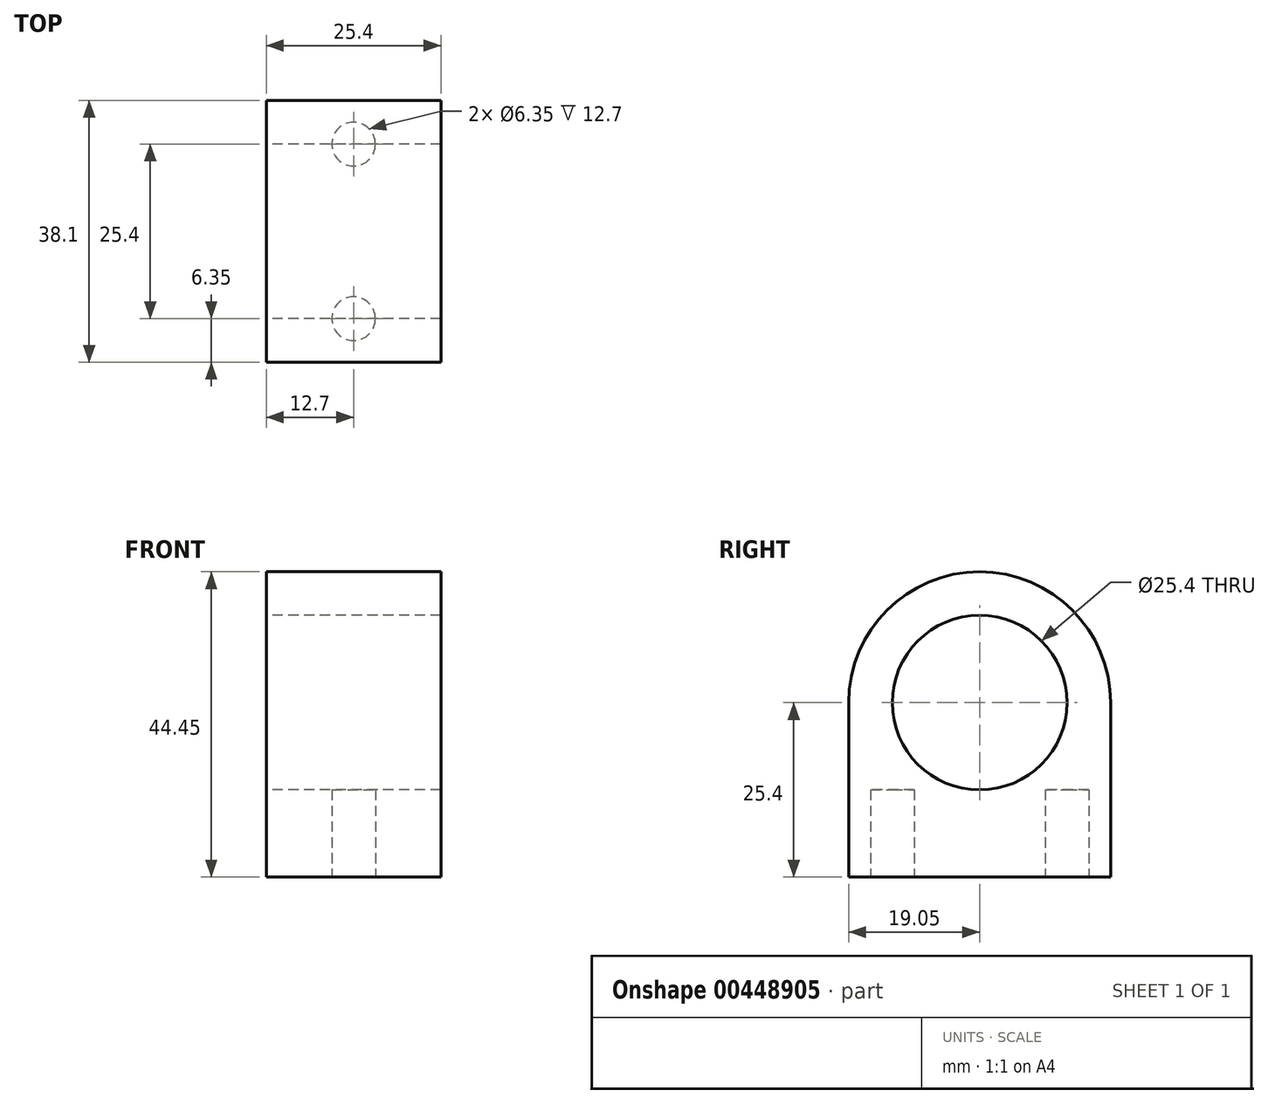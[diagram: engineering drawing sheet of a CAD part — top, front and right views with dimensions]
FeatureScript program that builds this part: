
annotation { "Feature Type Name" : "Feature", "Feature Type Description" : "" }
export const myFeature = defineFeature(function(context is Context, id is Id, definition is map)
    precondition{}
    {
        {
            var Q0;
            Q0=qCreatedBy(makeId("Right.planeOp"),FACE);
            var sketch = newSketch(context, id + "F0", { "sketchPlane" : qUnion([Q0])});
            skLineSegment(sketch, "E0", {"start": v(-19.05, 0) * mm, "end": v(-19.05, -25.4) * mm});
            skLineSegment(sketch, "E1", {"start": v(-19.05, -25.4) * mm, "end": v(19.05, -25.4) * mm});
            skLineSegment(sketch, "E2", {"start": v(19.05, -25.4) * mm, "end": v(19.05, 0) * mm});
            skArc(sketch, "E3", {"start": v(19.05, 0) * mm, "mid": v(0, 19.05) * mm, "end": v(-19.05, 0) * mm});
            skCircle(sketch, "E4", {"center": v(0, 0) * mm, "radius": 12.7 * mm});
            skSolve(sketch);
        }
        {
            var Q0;
            Q0=makeQuery(id+"F0.imprint","IMPRINT",FACE,{"disambiguationData":[TD([[makeQuery(id+"F0.imprint","IMPRINT",EDGE,{"derivedFrom":sQuery(id+"F0.wireOp",EDGE,"E0")}),1.0]])]});
            extrude(context, id + "F1", {"entities" : qUnion([Q0]), "endBound" : BoundingType.SYMMETRIC, "depth" : 25.4 * mm});
        }
        {
            var Q0;
            Q0=makeQuery(id+"F1.opExtrude","SWEPT_FACE",FACE,{"disambiguationData":[OSD([sQuery(id+"F0.wireOp",EDGE,"E1")])]});
            var sketch = newSketch(context, id + "F2", { "sketchPlane" : qUnion([Q0])});
            skCircle(sketch, "E5", {"center": v(0, 12.7) * mm, "radius": 3.18 * mm});
            skCircle(sketch, "E6", {"center": v(0, -12.7) * mm, "radius": 3.18 * mm});
            skSolve(sketch);
        }
        {
            var Q0;
            Q0 = qSketchRegion(id + "F2", true);
            extrude(context, id + "F3", {"entities" : qUnion([Q0]), "operationType" : NewBodyOperationType.REMOVE, "oppositeDirection" : true, "depth" : 12.7 * mm});
        }
    });
